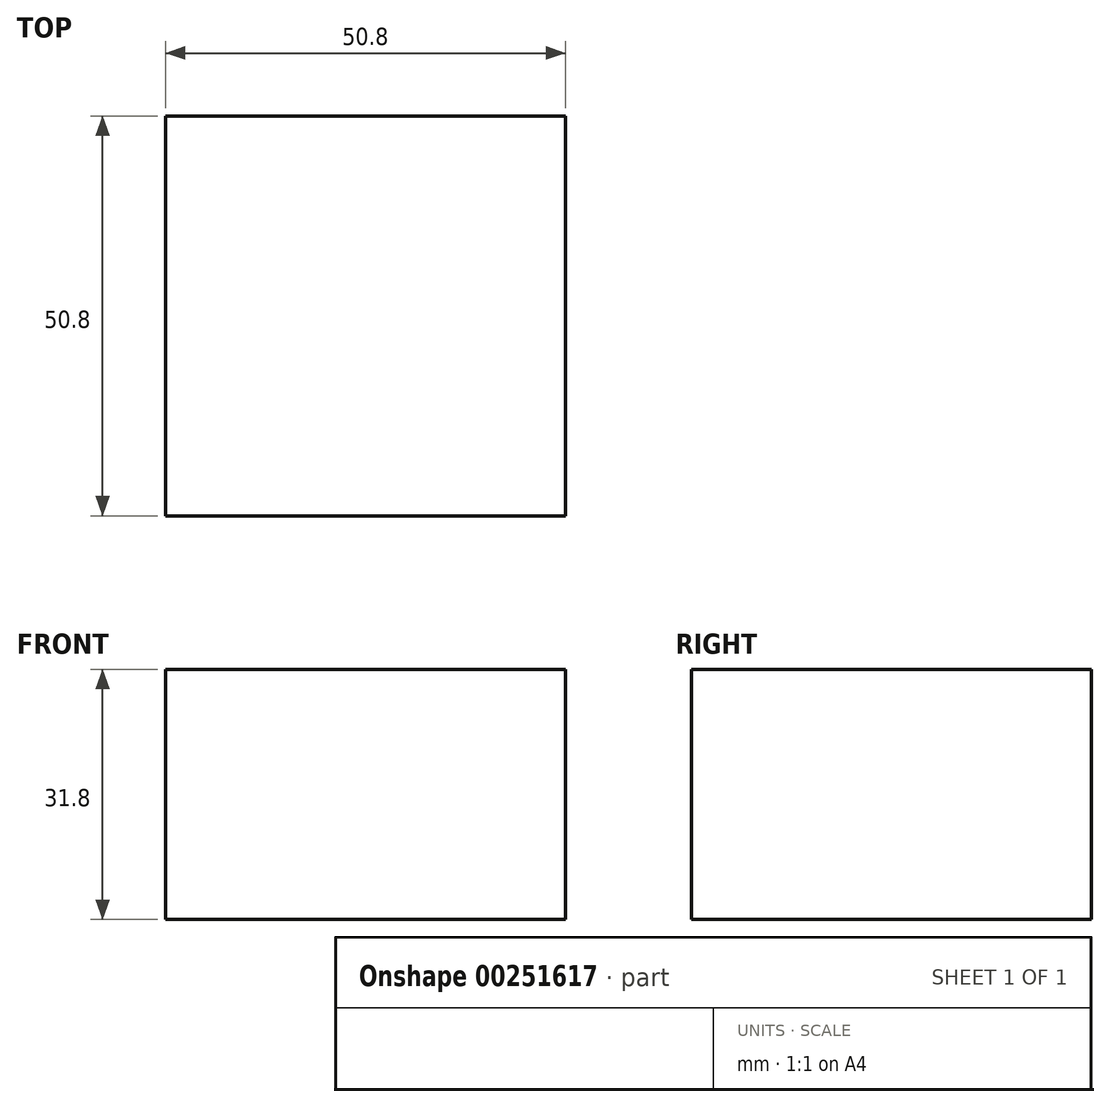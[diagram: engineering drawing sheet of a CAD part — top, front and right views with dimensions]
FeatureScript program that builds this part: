
annotation { "Feature Type Name" : "Feature", "Feature Type Description" : "" }
export const myFeature = defineFeature(function(context is Context, id is Id, definition is map)
    precondition{}
    {
        {
            var Q0;
            Q0=qCreatedBy(makeId("Front.planeOp"),FACE);
            var sketch = newSketch(context, id + "F0", { "sketchPlane" : qUnion([Q0])});
            skLineSegment(sketch, "E0.bottom", {"start": v(0, 0) * mm, "end": v(50.8, 0) * mm});
            skLineSegment(sketch, "E0.top", {"start": v(0, 31.8) * mm, "end": v(50.8, 31.8) * mm});
            skLineSegment(sketch, "E0.left", {"start": v(0, 0) * mm, "end": v(0, 31.8) * mm});
            skLineSegment(sketch, "E0.right", {"start": v(50.8, 0) * mm, "end": v(50.8, 31.8) * mm});
            skSolve(sketch);
        }
        {
            var Q0;
            Q0 = qSketchRegion(id + "F0", true);
            extrude(context, id + "F1", {"entities" : qUnion([Q0]), "depth" : 50.8 * mm});
        }
    });
